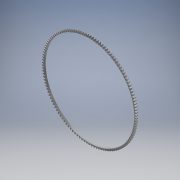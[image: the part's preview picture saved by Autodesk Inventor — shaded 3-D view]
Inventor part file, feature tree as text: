
AUTODESK INVENTOR PART (.ipt)
format: ipt  version: 2017 (Build 210142000, 142)  size: 650,752 bytes
history: native  units: mm (DEFAULTED — no unit token found)
features: plane x3, other x3, sketch x3, extrude x2
ambient origin geometry x8: Origin, YZ Plane, XZ Plane, XY Plane, X Axis, Y Axis, Z Axis, Center Point
bodies: Solid1 (feature_tree)
feature tree (11):
  extrude  "Extrusion1"  Depth=6.35mm TaperAngle=0.0deg
  plane  "Work Plane1"
  plane  "Work Plane2"
  plane  "Work Plane3"
  other  "Spur Gear"
  extrude  "Extrusion2"  Depth=76.2mm TaperAngle=0.0deg
  sketch  "Sketch1"  dims[d0=314.96mm d1=6.35mm d2=0.0mm]
  sketch  "Sketch2"  dims[d3=309.88mm d4=76.2mm d5=0.0mm]
  other  "Srf1"
  sketch  "Sketch3"  dims[d6=0.0mm d7=0.257508mm d9=0.0mm d14=0.0mm d15=173.99mm d16=0.0mm d17=0.0mm d18=0.0mm d19=173.99mm d20=302.26mm d21=25.4mm d22=0.0mm]
  other  "Pitch Diameter"
